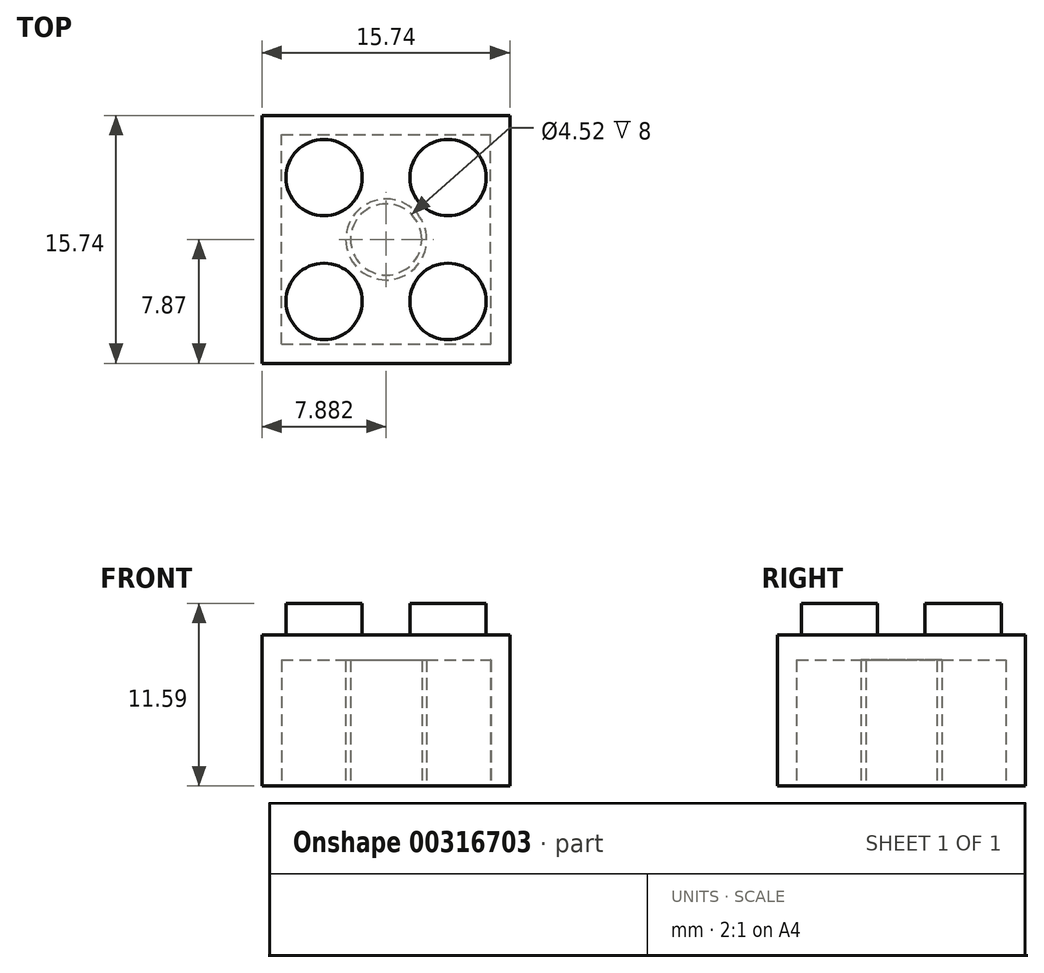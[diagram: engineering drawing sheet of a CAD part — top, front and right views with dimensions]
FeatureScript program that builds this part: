
annotation { "Feature Type Name" : "Feature", "Feature Type Description" : "" }
export const myFeature = defineFeature(function(context is Context, id is Id, definition is map)
    precondition{}
    {
        {
            var Q0;
            Q0=qCreatedBy(makeId("Top.planeOp"),FACE);
            var sketch = newSketch(context, id + "F0", { "sketchPlane" : qUnion([Q0])});
            skLineSegment(sketch, "E0.bottom", {"start": v(0, 0) * mm, "end": v(15.74, 0) * mm});
            skLineSegment(sketch, "E0.top", {"start": v(0, 15.74) * mm, "end": v(15.74, 15.74) * mm});
            skLineSegment(sketch, "E0.left", {"start": v(0, 0) * mm, "end": v(0, 15.74) * mm});
            skLineSegment(sketch, "E0.right", {"start": v(15.74, 0) * mm, "end": v(15.74, 15.74) * mm});
            skSolve(sketch);
        }
        {
            var Q0;
            Q0=makeQuery(id+"F0.imprint","IMPRINT",FACE,{"disambiguationData":[TD([[makeQuery(id+"F0.imprint","IMPRINT",EDGE,{"derivedFrom":sQuery(id+"F0.wireOp",EDGE,"E0.bottom")}),1.0]])]});
            extrude(context, id + "F1", {"entities" : qUnion([Q0]), "depth" : 9.6 * mm});
        }
        {
            var Q0;
            Q0=makeQuery(id+"F1.opExtrude","CAP_FACE",FACE,{"disambiguationData":[OSD([sQuery(id+"F0.wireOp",EDGE,"E0.bottom"),sQuery(id+"F0.wireOp",EDGE,"E0.top"),sQuery(id+"F0.wireOp",EDGE,"E0.left"),sQuery(id+"F0.wireOp",EDGE,"E0.right")])],"isStart":false});
            var sketch = newSketch(context, id + "F2", { "sketchPlane" : qUnion([Q0])});
            skLineSegment(sketch, "E1", {"start": v(7.87, 15.74) * mm, "end": v(7.87, 0) * mm});
            skLineSegment(sketch, "E2", {"start": v(7.87, 0) * mm, "end": v(0, 7.87) * mm});
            skLineSegment(sketch, "E3", {"start": v(0, 7.87) * mm, "end": v(15.74, 7.87) * mm});
            skLineSegment(sketch, "E4", {"start": v(15.74, 7.87) * mm, "end": v(7.87, 0) * mm});
            skLineSegment(sketch, "E5", {"start": v(7.87, 15.74) * mm, "end": v(0, 7.87) * mm});
            skLineSegment(sketch, "E6", {"start": v(7.87, 15.74) * mm, "end": v(15.74, 7.87) * mm});
            skCircle(sketch, "E7", {"center": v(3.94, 11.8) * mm, "radius": 2.43 * mm});
            skCircle(sketch, "E8", {"center": v(11.8, 11.8) * mm, "radius": 2.43 * mm});
            skCircle(sketch, "E9", {"center": v(11.8, 3.93) * mm, "radius": 2.43 * mm});
            skCircle(sketch, "E10", {"center": v(3.94, 3.93) * mm, "radius": 2.43 * mm});
            skSolve(sketch);
        }
        {
            var Q0;
            {var subQ0=sQuery(id+"F2.wireOp",EDGE,"E7");var subQ1=sQuery(id+"F2.wireOp",EDGE,"E5");var subQ2=makeQuery(id+"F2.imprint","INTERSECT",VERTEX,{"disambiguationData":[OD(0.0)],"derivedFrom":[subQ1,subQ0]});Q0=makeQuery(id+"F2.imprint","IMPRINT",FACE,{"disambiguationData":[TD([[makeQuery(id+"F2.imprint","IMPRINT",EDGE,{"disambiguationData":[TD([[subQ2,-1.0]])],"derivedFrom":subQ1}),1.0]])]});}
            var Q1;
            {var subQ0=sQuery(id+"F2.wireOp",EDGE,"E7");var subQ1=sQuery(id+"F2.wireOp",EDGE,"E5");var subQ2=makeQuery(id+"F2.imprint","INTERSECT",VERTEX,{"disambiguationData":[OD(0.0)],"derivedFrom":[subQ1,subQ0]});Q1=makeQuery(id+"F2.imprint","IMPRINT",FACE,{"disambiguationData":[TD([[makeQuery(id+"F2.imprint","IMPRINT",EDGE,{"disambiguationData":[TD([[subQ2,-1.0]])],"derivedFrom":subQ1}),-1.0]])]});}
            var Q2;
            {var subQ0=sQuery(id+"F2.wireOp",EDGE,"E8");var subQ1=sQuery(id+"F2.wireOp",EDGE,"E6");var subQ2=makeQuery(id+"F2.imprint","INTERSECT",VERTEX,{"disambiguationData":[OD(0.0)],"derivedFrom":[subQ1,subQ0]});Q2=makeQuery(id+"F2.imprint","IMPRINT",FACE,{"disambiguationData":[TD([[makeQuery(id+"F2.imprint","IMPRINT",EDGE,{"disambiguationData":[TD([[subQ2,-1.0]])],"derivedFrom":subQ1}),1.0]])]});}
            var Q3;
            {var subQ0=sQuery(id+"F2.wireOp",EDGE,"E8");var subQ1=sQuery(id+"F2.wireOp",EDGE,"E6");var subQ2=makeQuery(id+"F2.imprint","INTERSECT",VERTEX,{"disambiguationData":[OD(0.0)],"derivedFrom":[subQ1,subQ0]});Q3=makeQuery(id+"F2.imprint","IMPRINT",FACE,{"disambiguationData":[TD([[makeQuery(id+"F2.imprint","IMPRINT",EDGE,{"disambiguationData":[TD([[subQ2,-1.0]])],"derivedFrom":subQ1}),-1.0]])]});}
            var Q4;
            {var subQ0=sQuery(id+"F2.wireOp",EDGE,"E9");var subQ1=sQuery(id+"F2.wireOp",EDGE,"E4");var subQ2=makeQuery(id+"F2.imprint","INTERSECT",VERTEX,{"disambiguationData":[OD(0.0)],"derivedFrom":[subQ1,subQ0]});Q4=makeQuery(id+"F2.imprint","IMPRINT",FACE,{"disambiguationData":[TD([[makeQuery(id+"F2.imprint","IMPRINT",EDGE,{"disambiguationData":[TD([[subQ2,-1.0]])],"derivedFrom":subQ1}),1.0]])]});}
            var Q5;
            {var subQ0=sQuery(id+"F2.wireOp",EDGE,"E9");var subQ1=sQuery(id+"F2.wireOp",EDGE,"E4");var subQ2=makeQuery(id+"F2.imprint","INTERSECT",VERTEX,{"disambiguationData":[OD(0.0)],"derivedFrom":[subQ1,subQ0]});Q5=makeQuery(id+"F2.imprint","IMPRINT",FACE,{"disambiguationData":[TD([[makeQuery(id+"F2.imprint","IMPRINT",EDGE,{"disambiguationData":[TD([[subQ2,-1.0]])],"derivedFrom":subQ1}),-1.0]])]});}
            var Q6;
            {var subQ0=sQuery(id+"F2.wireOp",EDGE,"E10");var subQ1=sQuery(id+"F2.wireOp",EDGE,"E2");var subQ2=makeQuery(id+"F2.imprint","INTERSECT",VERTEX,{"disambiguationData":[OD(0.0)],"derivedFrom":[subQ1,subQ0]});Q6=makeQuery(id+"F2.imprint","IMPRINT",FACE,{"disambiguationData":[TD([[makeQuery(id+"F2.imprint","IMPRINT",EDGE,{"disambiguationData":[TD([[subQ2,-1.0]])],"derivedFrom":subQ1}),-1.0]])]});}
            var Q7;
            {var subQ0=sQuery(id+"F2.wireOp",EDGE,"E10");var subQ1=sQuery(id+"F2.wireOp",EDGE,"E2");var subQ2=makeQuery(id+"F2.imprint","INTERSECT",VERTEX,{"disambiguationData":[OD(0.0)],"derivedFrom":[subQ1,subQ0]});Q7=makeQuery(id+"F2.imprint","IMPRINT",FACE,{"disambiguationData":[TD([[makeQuery(id+"F2.imprint","IMPRINT",EDGE,{"disambiguationData":[TD([[subQ2,-1.0]])],"derivedFrom":subQ1}),1.0]])]});}
            extrude(context, id + "F3", {"entities" : qUnion([Q0, Q1, Q2, Q3, Q4, Q5, Q6, Q7]), "operationType" : NewBodyOperationType.ADD, "depth" : 2 * mm});
        }
        {
            var Q0;
            Q0=makeQuery(id+"F1.opExtrude","CAP_FACE",FACE,{"disambiguationData":[OSD([sQuery(id+"F0.wireOp",EDGE,"E0.bottom"),sQuery(id+"F0.wireOp",EDGE,"E0.top"),sQuery(id+"F0.wireOp",EDGE,"E0.left"),sQuery(id+"F0.wireOp",EDGE,"E0.right")])],"isStart":true});
            var sketch = newSketch(context, id + "F4", { "sketchPlane" : qUnion([Q0])});
            skLineSegment(sketch, "E11", {"start": v(1.22, -1.22) * mm, "end": v(1.22, -14.52) * mm});
            skLineSegment(sketch, "E12", {"start": v(1.22, -14.52) * mm, "end": v(14.5, -14.52) * mm});
            skLineSegment(sketch, "E13", {"start": v(1.22, -1.22) * mm, "end": v(14.54, -1.22) * mm});
            skLineSegment(sketch, "E14", {"start": v(14.54, -1.22) * mm, "end": v(14.5, -14.52) * mm});
            skCircle(sketch, "E15", {"center": v(7.88, -7.87) * mm, "radius": 2.57 * mm});
            skCircle(sketch, "E16", {"center": v(7.88, -7.87) * mm, "radius": 2.26 * mm});
            skSolve(sketch);
        }
        {
            var Q0;
            Q0=makeQuery(id+"F4.imprint","IMPRINT",FACE,{"disambiguationData":[TD([[makeQuery(id+"F4.imprint","IMPRINT",EDGE,{"derivedFrom":sQuery(id+"F4.wireOp",EDGE,"E11")}),1.0]])]});
            extrude(context, id + "F5", {"entities" : qUnion([Q0]), "operationType" : NewBodyOperationType.REMOVE, "oppositeDirection" : true, "depth" : 8 * mm});
        }
        {
            var Q0;
            Q0=makeQuery(id+"F4.imprint","IMPRINT",FACE,{"disambiguationData":[TD([[makeQuery(id+"F4.imprint","IMPRINT",EDGE,{"derivedFrom":sQuery(id+"F4.wireOp",EDGE,"E16")}),1.0]])]});
            extrude(context, id + "F6", {"entities" : qUnion([Q0]), "operationType" : NewBodyOperationType.REMOVE, "oppositeDirection" : true, "depth" : 8 * mm});
        }
    });
